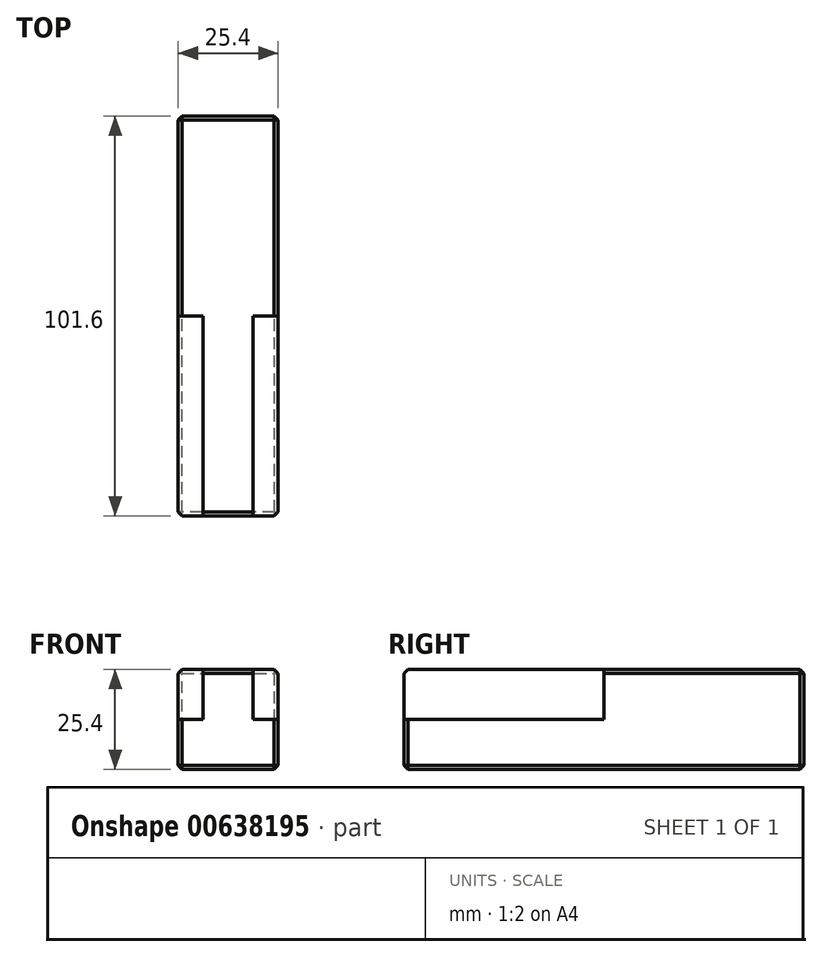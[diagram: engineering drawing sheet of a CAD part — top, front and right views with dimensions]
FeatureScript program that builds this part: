
annotation { "Feature Type Name" : "Feature", "Feature Type Description" : "" }
export const myFeature = defineFeature(function(context is Context, id is Id, definition is map)
    precondition{}
    {
        {
            var Q0;
            Q0=qCreatedBy(makeId("Front.planeOp"),FACE);
            var sketch = newSketch(context, id + "F0", { "sketchPlane" : qUnion([Q0])});
            skLineSegment(sketch, "E0.bottom", {"start": v(12.7, -12.7) * mm, "end": v(-12.7, -12.7) * mm});
            skLineSegment(sketch, "E0.top", {"start": v(12.7, 12.7) * mm, "end": v(-12.7, 12.7) * mm});
            skLineSegment(sketch, "E0.left", {"start": v(12.7, -12.7) * mm, "end": v(12.7, 12.7) * mm});
            skLineSegment(sketch, "E0.right", {"start": v(-12.7, -12.7) * mm, "end": v(-12.7, 12.7) * mm});
            skPoint(sketch, "E0.middle", {"position": v(0, 0) * mm});
            skSolve(sketch);
        }
        {
            var Q0;
            Q0=makeQuery(id+"F0.imprint","IMPRINT",FACE,{"disambiguationData":[TD([[makeQuery(id+"F0.imprint","IMPRINT",EDGE,{"derivedFrom":sQuery(id+"F0.wireOp",EDGE,"E0.bottom")}),-1.0]])]});
            extrude(context, id + "F1", {"entities" : qUnion([Q0]), "endBound" : BoundingType.SYMMETRIC, "depth" : (25.4 * 4) * mm, "offsetDistance" : 25 * mm});
        }
        {
            var Q0;
            Q0=makeQuery(id+"F1.opExtrude","CAP_FACE",FACE,{"disambiguationData":[OSD([sQuery(id+"F0.wireOp",EDGE,"E0.bottom"),sQuery(id+"F0.wireOp",EDGE,"E0.top"),sQuery(id+"F0.wireOp",EDGE,"E0.left"),sQuery(id+"F0.wireOp",EDGE,"E0.right")])],"isStart":false});
            var sketch = newSketch(context, id + "F2", { "sketchPlane" : qUnion([Q0])});
            skLineSegment(sketch, "E1.bottom", {"start": v(12.7, 12.7) * mm, "end": v(6.35, 12.7) * mm});
            skLineSegment(sketch, "E1.top", {"start": v(12.7, 0) * mm, "end": v(6.35, 0) * mm});
            skLineSegment(sketch, "E1.left", {"start": v(12.7, 12.7) * mm, "end": v(12.7, 0) * mm});
            skLineSegment(sketch, "E1.right", {"start": v(6.35, 12.7) * mm, "end": v(6.35, 0) * mm});
            skLineSegment(sketch, "E2.bottom", {"start": v(-12.7, 12.7) * mm, "end": v(-6.35, 12.7) * mm});
            skLineSegment(sketch, "E2.top", {"start": v(-12.7, 0) * mm, "end": v(-6.35, 0) * mm});
            skLineSegment(sketch, "E2.left", {"start": v(-12.7, 12.7) * mm, "end": v(-12.7, 0) * mm});
            skLineSegment(sketch, "E2.right", {"start": v(-6.35, 12.7) * mm, "end": v(-6.35, 0) * mm});
            skSolve(sketch);
        }
        {
            var Q0;
            Q0=makeQuery(id+"F2.imprint","IMPRINT",FACE,{"disambiguationData":[TD([[makeQuery(id+"F2.imprint","IMPRINT",EDGE,{"derivedFrom":sQuery(id+"F2.wireOp",EDGE,"E2.bottom")}),1.0]])]});
            var Q1;
            Q1=makeQuery(id+"F2.imprint","IMPRINT",FACE,{"disambiguationData":[TD([[makeQuery(id+"F2.imprint","IMPRINT",EDGE,{"derivedFrom":sQuery(id+"F2.wireOp",EDGE,"E1.bottom")}),1.0]])]});
            extrude(context, id + "F3", {"entities" : qUnion([Q0, Q1]), "operationType" : NewBodyOperationType.REMOVE, "oppositeDirection" : true, "depth" : (25.4 * 2) * mm, "offsetDistance" : 25 * mm});
        }
        {
            var Q0;
            Q0=makeQuery(id+"F1.opExtrude","SWEPT_EDGE",EDGE,{"disambiguationData":[OSD([sQuery(id+"F0.wireOp",EDGE,"E0.top"),sQuery(id+"F0.wireOp",EDGE,"E0.left")])]});
            var Q1;
            Q1=makeQuery(id+"F1.opExtrude","SWEPT_EDGE",EDGE,{"disambiguationData":[OSD([sQuery(id+"F0.wireOp",EDGE,"E0.bottom"),sQuery(id+"F0.wireOp",EDGE,"E0.left")])]});
            var Q2;
            Q2=makeQuery(id+"F1.opExtrude","CAP_EDGE",EDGE,{"disambiguationData":[OSD([sQuery(id+"F0.wireOp",EDGE,"E0.left")])],"isStart":true});
            var Q3;
            Q3=makeQuery(id+"F1.opExtrude","CAP_EDGE",EDGE,{"disambiguationData":[OSD([sQuery(id+"F0.wireOp",EDGE,"E0.left")])],"isStart":false});
            var Q4;
            Q4=makeQuery(id+"F1.opExtrude","CAP_EDGE",EDGE,{"disambiguationData":[OSD([sQuery(id+"F0.wireOp",EDGE,"E0.top")])],"isStart":false});
            var Q5;
            Q5=makeQuery(id+"F1.opExtrude","CAP_EDGE",EDGE,{"disambiguationData":[OSD([sQuery(id+"F0.wireOp",EDGE,"E0.right")])],"isStart":false});
            var Q6;
            Q6=makeQuery(id+"F1.opExtrude","SWEPT_EDGE",EDGE,{"disambiguationData":[OSD([sQuery(id+"F0.wireOp",EDGE,"E0.top"),sQuery(id+"F0.wireOp",EDGE,"E0.right")])]});
            var Q7;
            Q7=makeQuery(id+"F1.opExtrude","CAP_EDGE",EDGE,{"disambiguationData":[OSD([sQuery(id+"F0.wireOp",EDGE,"E0.top")])],"isStart":true});
            var Q8;
            Q8=makeQuery(id+"F1.opExtrude","CAP_EDGE",EDGE,{"disambiguationData":[OSD([sQuery(id+"F0.wireOp",EDGE,"E0.bottom")])],"isStart":false});
            var Q9;
            Q9=makeQuery(id+"F1.opExtrude","SWEPT_EDGE",EDGE,{"disambiguationData":[OSD([sQuery(id+"F0.wireOp",EDGE,"E0.bottom"),sQuery(id+"F0.wireOp",EDGE,"E0.right")])]});
            var Q10;
            Q10=makeQuery(id+"F1.opExtrude","CAP_EDGE",EDGE,{"disambiguationData":[OSD([sQuery(id+"F0.wireOp",EDGE,"E0.right")])],"isStart":true});
            var Q11;
            Q11=makeQuery(id+"F1.opExtrude","CAP_EDGE",EDGE,{"disambiguationData":[OSD([sQuery(id+"F0.wireOp",EDGE,"E0.bottom")])],"isStart":true});
            chamfer(context, id + "F4", {"entities" : qUnion([Q0, Q1, Q2, Q3, Q4, Q5, Q6, Q7, Q8, Q9, Q10, Q11]), "width" : 1 * mm, "tangentPropagation" : true});
        }
    });
